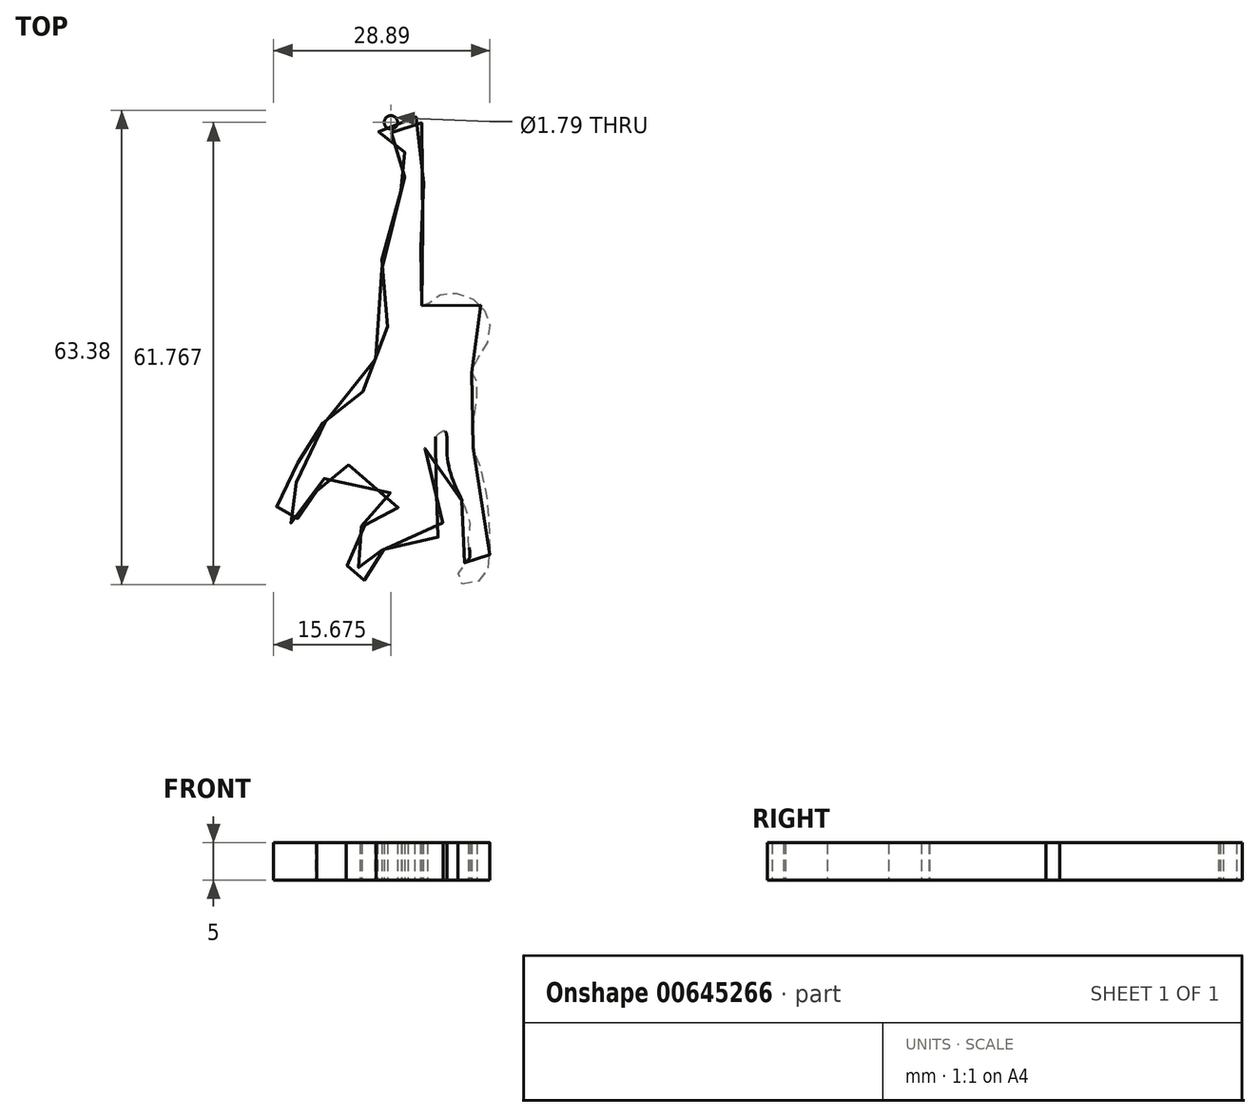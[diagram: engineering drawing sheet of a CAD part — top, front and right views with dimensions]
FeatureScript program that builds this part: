
annotation { "Feature Type Name" : "Feature", "Feature Type Description" : "" }
export const myFeature = defineFeature(function(context is Context, id is Id, definition is map)
    precondition{}
    {
        {
            var Q0;
            Q0=qCreatedBy(makeId("Top.planeOp"),FACE);
            var sketch = newSketch(context, id + "F0", { "sketchPlane" : qUnion([Q0])});
            skFitSpline(sketch, "E0", {"points": [v(22.73, 39.44) * mm, v(23.47, 39.54) * mm, v(25.4, 41) * mm, v(29.33, 40.45) * mm, v(31.53, 37.98) * mm, v(31.35, 34.22) * mm, v(29.33, 30.74) * mm, v(29.88, 29.82) * mm, v(29.8, 25.15) * mm, v(29.52, 20.93) * mm, v(30.9, 16.71) * mm, v(31.8, 6.9) * mm, v(30.62, 2.78) * mm, v(27.68, 2.5) * mm, v(28.32, 4.9) * mm, v(29.15, 5.8) * mm, v(28.97, 8.28) * mm, v(29.15, 10.67) * mm, v(26.22, 18.64) * mm, v(25.67, 22.67) * mm, v(22.55, 19.28) * mm, v(23, 18.91) * mm, v(25.4, 13.5) * mm, v(25.3, 9.3) * mm, v(24.3, 8) * mm, v(19.62, 7.37) * mm, v(16.5, 5.8) * mm, v(16.6, 3.8) * mm, v(14.94, 2.78) * mm, v(14.58, 3.98) * mm, v(13.94, 4.53) * mm, v(12.65, 4.34) * mm, v(14.67, 7.73) * mm, v(14.49, 9.75) * mm, v(17.14, 10.4) * mm, v(20.08, 11.86) * mm, v(19.53, 12.5) * mm, v(17.05, 16.35) * mm, v(11, 18.27) * mm, v(10.73, 17.72) * mm, v(8.62, 14.42) * mm, v(8.62, 12.13) * mm, v(7.43, 11.77) * mm, v(5.23, 10.4) * mm, v(3.58, 10.3) * mm, v(3.03, 12.04) * mm, v(5.6, 14.7) * mm, v(6.05, 17.81) * mm, v(7.15, 21.02) * mm, v(8.62, 23.59) * mm, v(13.57, 24.05) * mm, v(15.04, 28.81) * mm, v(17.97, 35.32) * mm, v(17.78, 39.26) * mm, v(17.5, 46.6) * mm, v(19.34, 53.47) * mm, v(20.44, 56.77) * mm, v(19.98, 59.06) * mm, v(20.53, 60.07) * mm, v(20.53, 62.54) * mm, v(17.14, 62.54) * mm, v(17.6, 64.92) * mm, v(21.45, 65.01) * mm, v(23.47, 61.44) * mm, v(22.73, 53.1) * mm, v(22.83, 47.97) * mm, v(21.82, 44.76) * mm, v(22.73, 39.44) * mm]});
            skSolve(sketch);
        }
        {
            var Q0;
            Q0=makeQuery(id+"F0.imprint","IMPRINT",FACE,{"disambiguationData":[TD([[makeQuery(id+"F0.imprint","IMPRINT",EDGE,{"derivedFrom":sQuery(id+"F0.wireOp",EDGE,"E0")}),-1.0]])]});
            var sketch = newSketch(context, id + "F1", { "sketchPlane" : qUnion([Q0])});
            skCircle(sketch, "E1", {"center": v(18.61, 63.93) * mm, "radius": 0.9 * mm});
            skSolve(sketch);
        }
        {
            var Q0;
            Q0=makeQuery(id+"F1.imprint","IMPRINT",FACE,{"disambiguationData":[TD([[makeQuery(id+"F1.imprint","IMPRINT",EDGE,{"derivedFrom":sQuery(id+"F1.wireOp",EDGE,"E1")}),-1.0]])]});
            extrude(context, id + "F2", {"entities" : qUnion([Q0]), "depth" : 5 * mm, "offsetDistance" : 25 * mm});
        }
        {
            var Q0;
            Q0=qCreatedBy(makeId("Top.planeOp"),FACE);
            var sketch = newSketch(context, id + "F3", { "sketchPlane" : qUnion([Q0])});
            skCircle(sketch, "E2", {"center": v(26.07, 38.38) * mm, "radius": 1.01 * mm});
            skCircle(sketch, "E3", {"center": v(28.93, 36.13) * mm, "radius": 1 * mm});
            skSolve(sketch);
        }
        {
            var Q0;
            Q0 = qSketchRegion(id + "F3", true);
            extrude(context, id + "F4", {"entities" : qUnion([Q0]), "operationType" : NewBodyOperationType.REMOVE, "oppositeDirection" : true, "depth" : 5 * mm, "offsetDistance" : 25 * mm});
        }
    });
